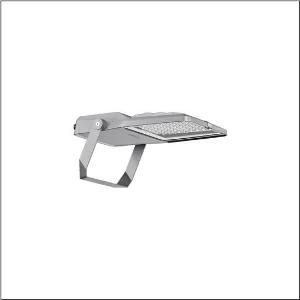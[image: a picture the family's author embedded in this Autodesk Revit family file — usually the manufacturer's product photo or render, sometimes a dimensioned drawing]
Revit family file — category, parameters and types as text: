
# Revit family: floodlight_fl_21_mini___pl43_5xa7775c2a1a_0644
name_source: partatom
category: Lighting Fixtures
units: mm (PartAtom-declared; Revit-internal decimal feet)

## family parameters
Cut with Voids When Loaded = No
Host = Face
Light Source = No
Part Type = Normal
Room Calculation Point = No
Round Connector Dimension = Use Diameter
Shared = No

## types (1)
- --- (1 x LED, 12500 lm, 89 W, 3000K)
    Apparent Load = 89 VA
    CIE Flux Codes = 27 78 99 100 100
    Color Rendering = 70
    Color Temperature = 3000K
    Default Elevation = 1800 mm
    Description = Floodlight FL 21 mini, floodlight, primary light control with lens, of PMMA, primary optical cover: protective disc, of toughened safety glass, transparent, light distribution: PL43, light emission: direct distribution, installation type: surface-mounted, LED, High Power LED, rated luminous flux: 12.500lm, luminous efficacy: 140lm/W, light colour: 730, colour temperature: 3000K, control gear: Smart Interface (Zhaga), control: flexible luminous flux parameterisation, time-dependent luminous flux control, constant luminous flux control, overheat protection, pre-setting: logarithmic dimming characteristic, with terminal, 6-pole, mains connection: 220..240V, AC, 50/60Hz, start of lifetime: 89W, end of service life: 94W, reduction: 43W, luminaire housing, of diecast aluminium, powder-coated, SITECO metallic grey (DB 702S), corrosivity category C5 mid according to DIN EN ISO 12944, suitable for swimming pools, chlorine-resistant, sealing non-destructively replaceable, mounting bracket, of steel, galvanised, powder-coated, SITECO metallic grey (DB 702S), Smart Interface above, protection rating (complete): IP66, insulation class (complete): insulation class II (safety insulation), certification: CE, ENEC, VDE, protection symbol: D, impact resistance: IK08, permissible operating ambient temperature: -40..+40°C, permissible operating ambient temperature for outdoor applications: -40..+50°C, standard: DIN EN 12944, LABS conformity tested according to VDMA 24364:2018-05, packaging unit: 1 piece

Light Distribution: PL43
    Height = 70 mm
    Lamp = 1 x LED
    Lamp Light Flux = 12500 lm
    Lamp Power = 89 W
    Lamp count = 1
    Length = 485 mm
    Luminous efficacy = 140 lm/W
    Manufacturer = Siteco
    ModVariant = No
    Model = 5XA7775C2A1A
    Mounting Place = Pole
    Mounting Type = Pole annexe
    Number of Poles = 1
    OnlyDefault = Yes
    Power Factor = 1
    Product Name = Floodlight FL 21 mini | PL43
    Product group = floodlight | pylon annexe
    ProductGroupID = 6201
    Protection Class = Protection class II
    Protection Degree = IP 66
    RLX_Detail_Level = 1
    RLX_Emergency_Light_Flux = 0 lm
    RLX_Emergency_Type = 0
    RLX_Emergency_Type_DB = No
    RlxData = <blob elided: 95817 chars, md5=3cc6d781>
    Socket = socket
    Standby Power = 0 W
    System Light Flux = 12500 lm
    System Power = 89 W
    Type Comments = factory setting: luminous flux: 100 % | dim-lin: 254 | 456 mA
    Type Image = l_1006845.jpg
    URL = http://relux.com
    VarID = @adj_162207
    Voltage = 0 V
    Weight = 0.00 kg
    Width = 337 mm

## geometry (parser evidence)
native form markers: Blend x4, Sweep x10
no freeform markers — native parametric forms only
